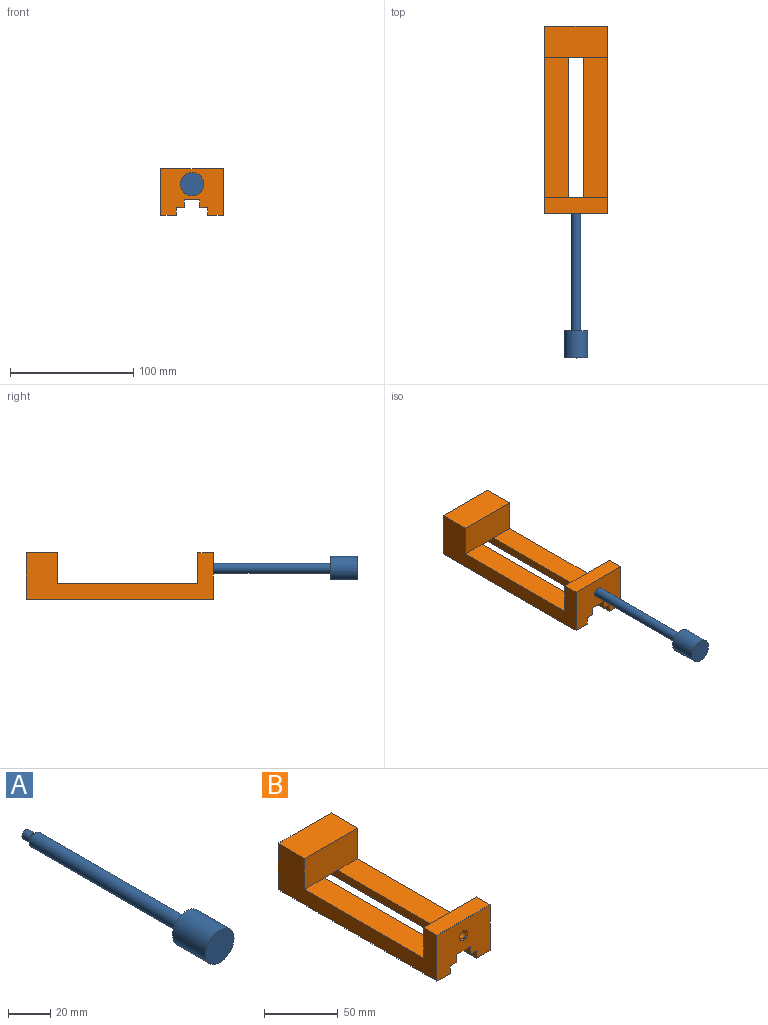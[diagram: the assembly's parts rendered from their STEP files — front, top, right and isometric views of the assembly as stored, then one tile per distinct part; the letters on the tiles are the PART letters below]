
ASSEMBLY  parts=2 mates=1
PART A: 11 faces, bbox 19.1x130.2x19.1 mm
  f0: cylinder r=9.53mm len=22.23mm, axis (0,1,0), area 1330.1mm2, adj f1,f10
  f1: plane 19.05x19.05mm, normal (0,-1,0), area 285mm2, adj f0
  f2: plane 5.08x5.08mm, normal (0,1,0), area 20.3mm2, adj f3
  f3: cylinder r=2.54mm len=5.08mm, axis (0,1,0), area 75.8mm2, adj f2,f4
  f4: plane 5.08x5.08mm, normal (0,-1,0), area 15.2mm2, adj f3,f5
  f5: cylinder r=1.27mm len=6.35mm, axis (0,1,0), area 50.7mm2, adj f4,f6
  f6: plane 5.08x5.08mm, normal (0,1,0), area 15.2mm2, adj f5,f7
  f7: cylinder r=2.54mm len=5.08mm, axis (0,1,0), area 75.8mm2, adj f6,f8
  f8: plane 7.92x7.92mm, normal (0,1,0), area 29.1mm2, adj f7,f9
  f9: cylinder r=3.96mm len=101.6mm, axis (0,1,0), area 2529.5mm2, adj f8,f10
  f10: plane 19.05x19.05mm, normal (0,1,0), area 235.7mm2, adj f0,f9
PART B: 22 faces, bbox 50.8x152.4x38.1 mm
  f0: plane 114.3x19.05mm, normal (0,0,1), area 2177.4mm2, adj f3,f9,f11,f17
  f1: plane 152.4x12.7mm, normal (0,0,-1), area 1935.5mm2, adj f5,f7,f10,f13
  f2: plane 114.3x19.05mm, normal (0,0,1), area 2177.4mm2, adj f3,f9,f10,f15
  f3: plane 50.8x25.4mm, normal (0,1,0), area 1260.9mm2, adj f0,f2,f4,f10,f11,f16,f20
  f4: plane 50.8x12.7mm, normal (0,0,1), area 645.2mm2, adj f3,f5,f10,f11
  f5: plane 50.8x38.1mm, normal (0,-1,0), area 1647mm2, adj f1,f4,f6,f10,f11,f13,f14,f15
  f6: plane 152.4x12.7mm, normal (0,0,-1), area 1935.5mm2, adj f5,f7,f11,f19
  f7: plane 50.8x38.1mm, normal (0,1,0), area 1693.5mm2, adj f1,f6,f8,f10,f11,f12,f13,f14
  f8: plane 50.8x25.4mm, normal (0,0,1), area 1290.3mm2, adj f7,f9,f10,f11
  f9: plane 50.8x25.4mm, normal (0,-1,0), area 1290.3mm2, adj f0,f2,f8,f10,f11,f12
  f10: plane 152.4x38.1mm, normal (1,0,0), area 2903.2mm2, adj f1,f2,f3,f4,f5,f7,f8,f9
  f11: plane 152.4x38.1mm, normal (-1,0,0), area 2903.2mm2, adj f0,f3,f4,f5,f6,f7,f8,f9
  f12: plane 25.4x12.7mm, normal (0,0,-1), area 322.6mm2, adj f7,f9,f15,f17
  f13: plane 152.4x6.35mm, normal (-1,0,0), area 967.7mm2, adj f1,f5,f7,f14
  f14: plane 152.4x6.35mm, normal (0,0,-1), area 967.7mm2, adj f5,f7,f13,f15
  f15: plane 152.4x6.35mm, normal (-1,0,0), area 967.7mm2, adj f2,f5,f7,f12,f14,f16
  f16: plane 12.7x12.7mm, normal (0,0,-1), area 161.3mm2, adj f3,f5,f15,f17
  f17: plane 152.4x6.35mm, normal (1,0,0), area 967.7mm2, adj f0,f5,f7,f12,f16,f18
  f18: plane 152.4x6.35mm, normal (0,0,-1), area 967.7mm2, adj f5,f7,f17,f19
  f19: plane 152.4x6.35mm, normal (1,0,0), area 967.7mm2, adj f5,f6,f7,f18
  f20: cylinder r=3.06mm len=11.91mm, axis (0,-1,0), area 229.2mm2, adj f3,f21
  f21: cone r=3.06mm half-angle=45deg, axis (0,-1,0), area 24.2mm2, adj f5,f20
PLACE A rot(axis=(0,-1,0),5.5deg) t=(5.74,-18.36,15.06)mm
PLACE B t=(3.3,-13.53,14.94)mm fixed
MATE revolute B.f21 <-> A.f0  axis (0,1,0) through (3.3,-38.93,40.34)mm
